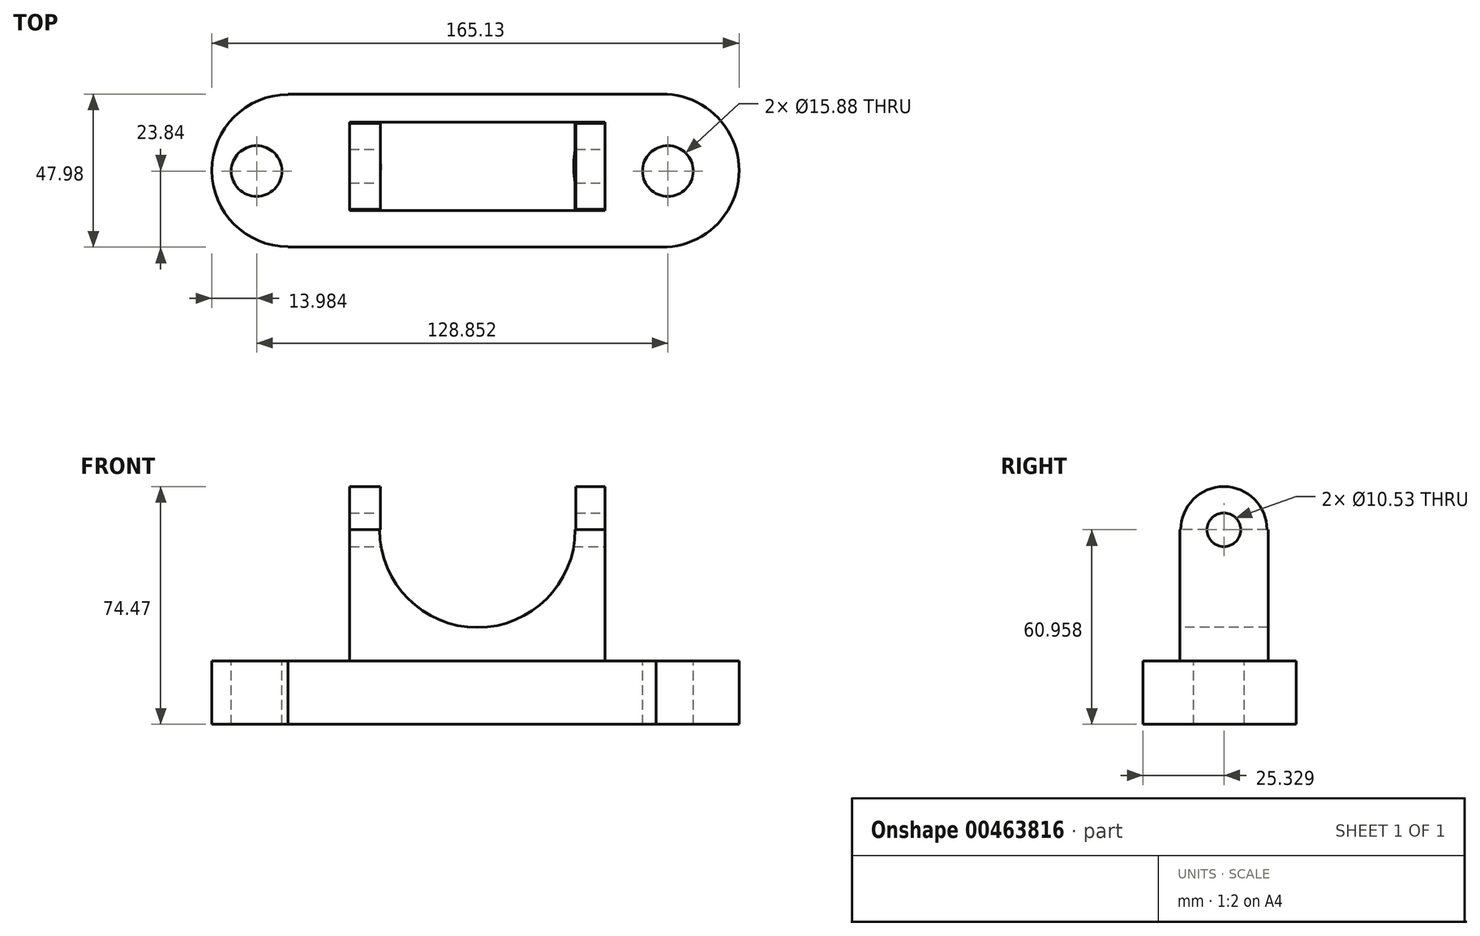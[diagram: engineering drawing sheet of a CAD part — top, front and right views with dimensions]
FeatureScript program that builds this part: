
annotation { "Feature Type Name" : "Feature", "Feature Type Description" : "" }
export const myFeature = defineFeature(function(context is Context, id is Id, definition is map)
    precondition{}
    {
        {
            var Q0;
            Q0=qCreatedBy(makeId("Top.planeOp"),FACE);
            var sketch = newSketch(context, id + "F0", { "sketchPlane" : qUnion([Q0])});
            skLineSegment(sketch, "E0.bottom", {"start": v(-54.58, 24.06) * mm, "end": v(62.72, 24.06) * mm});
            skLineSegment(sketch, "E0.top", {"start": v(-54.58, -23.76) * mm, "end": v(62.72, -23.76) * mm});
            skLineSegment(sketch, "E0.left", {"start": v(-54.58, 24.06) * mm, "end": v(-54.58, -23.76) * mm});
            skLineSegment(sketch, "E0.right", {"start": v(62.72, 24.06) * mm, "end": v(62.72, -23.76) * mm});
            skCircle(sketch, "E1", {"center": v(-54.58, 0.15) * mm, "radius": 23.83 * mm});
            skCircle(sketch, "E2", {"center": v(62.72, 0.15) * mm, "radius": 24 * mm});
            skSolve(sketch);
        }
        {
            var Q0;
            {var subQ0=sQuery(id+"F0.wireOp",EDGE,"E0.right");Q0=makeQuery(id+"F0.imprint","IMPRINT",FACE,{"disambiguationData":[TD([[makeQuery(id+"F0.imprint","IMPRINT",EDGE,{"derivedFrom":subQ0}),-1.0]])]});}
            var Q1;
            {var subQ0=sQuery(id+"F0.wireOp",EDGE,"E0.left");var subQ5=sQuery(id+"F0.wireOp",EDGE,"E0.bottom");var subQ6=makeQuery(id+"F0.imprint","INTERSECT",VERTEX,{"derivedFrom":[subQ5,subQ0]});Q1=makeQuery(id+"F0.imprint","IMPRINT",FACE,{"disambiguationData":[TD([[makeQuery(id+"F0.imprint","IMPRINT",EDGE,{"disambiguationData":[TD([[subQ6,-1.0]])],"derivedFrom":subQ5}),-1.0]])]});}
            var Q2;
            {var subQ0=sQuery(id+"F0.wireOp",EDGE,"E1");var subQ1=sQuery(id+"F0.wireOp",EDGE,"E0.left");var subQ2=makeQuery(id+"F0.imprint","INTERSECT",VERTEX,{"disambiguationData":[OD(0.0)],"derivedFrom":[subQ1,subQ0]});Q2=makeQuery(id+"F0.imprint","IMPRINT",FACE,{"disambiguationData":[TD([[makeQuery(id+"F0.imprint","IMPRINT",EDGE,{"disambiguationData":[TD([[subQ2,-1.0]])],"derivedFrom":subQ1}),-1.0]])]});}
            var Q3;
            {var subQ0=sQuery(id+"F0.wireOp",EDGE,"E0.right");Q3=makeQuery(id+"F0.imprint","IMPRINT",FACE,{"disambiguationData":[TD([[makeQuery(id+"F0.imprint","IMPRINT",EDGE,{"derivedFrom":subQ0}),1.0]])]});}
            var Q4;
            {var subQ0=sQuery(id+"F0.wireOp",EDGE,"E1");var subQ1=sQuery(id+"F0.wireOp",EDGE,"E0.left");var subQ2=makeQuery(id+"F0.imprint","INTERSECT",VERTEX,{"disambiguationData":[OD(0.0)],"derivedFrom":[subQ1,subQ0]});Q4=makeQuery(id+"F0.imprint","IMPRINT",FACE,{"disambiguationData":[TD([[makeQuery(id+"F0.imprint","IMPRINT",EDGE,{"disambiguationData":[TD([[subQ2,-1.0]])],"derivedFrom":subQ1}),1.0]])]});}
            extrude(context, id + "F1", {"entities" : qUnion([Q0, Q1, Q2, Q3, Q4]), "oppositeDirection" : true, "depth" : 19.8 * mm});
        }
        {
            var Q0;
            Q0=makeQuery(id+"F1.opExtrude","CAP_FACE",FACE,{"disambiguationData":[OSD([sQuery(id+"F0.wireOp",EDGE,"E0.bottom"),sQuery(id+"F0.wireOp",EDGE,"E0.top"),sQuery(id+"F0.wireOp",EDGE,"E0.left"),sQuery(id+"F0.wireOp",EDGE,"E1"),sQuery(id+"F0.wireOp",EDGE,"E2")])],"isStart":true});
            var sketch = newSketch(context, id + "F2", { "sketchPlane" : qUnion([Q0])});
            skCircle(sketch, "E3", {"center": v(-64.43, 0) * mm, "radius": 7.94 * mm});
            skCircle(sketch, "E4.MirrorC", {"center": v(64.43, 0) * mm, "radius": 7.94 * mm});
            skSolve(sketch);
        }
        {
            var Q0;
            Q0=makeQuery(id+"F2.imprint","IMPRINT",FACE,{"disambiguationData":[TD([[makeQuery(id+"F2.imprint","IMPRINT",EDGE,{"derivedFrom":sQuery(id+"F2.wireOp",EDGE,"E3")}),1.0]])]});
            extrude(context, id + "F3", {"entities" : qUnion([Q0]), "operationType" : NewBodyOperationType.REMOVE, "oppositeDirection" : true, "depth" : 53.6 * mm});
        }
        {
            var Q0;
            Q0 = qSketchRegion(id + "F2", true);
            extrude(context, id + "F4", {"entities" : qUnion([Q0]), "operationType" : NewBodyOperationType.REMOVE, "oppositeDirection" : true, "depth" : 72.14 * mm});
        }
        {
            var Q0;
            Q0=makeQuery(id+"F1.opExtrude","CAP_FACE",FACE,{"disambiguationData":[OSD([sQuery(id+"F0.wireOp",EDGE,"E0.bottom"),sQuery(id+"F0.wireOp",EDGE,"E0.top"),sQuery(id+"F0.wireOp",EDGE,"E0.left"),sQuery(id+"F0.wireOp",EDGE,"E1"),sQuery(id+"F0.wireOp",EDGE,"E2")])],"isStart":true});
            var sketch = newSketch(context, id + "F5", { "sketchPlane" : qUnion([Q0])});
            skLineSegment(sketch, "E5.bottom", {"start": v(-35.25, 15.31) * mm, "end": v(44.76, 15.31) * mm});
            skLineSegment(sketch, "E5.top", {"start": v(-35.25, -12.34) * mm, "end": v(44.76, -12.34) * mm});
            skLineSegment(sketch, "E5.left", {"start": v(-35.25, 15.31) * mm, "end": v(-35.25, -12.34) * mm});
            skLineSegment(sketch, "E5.right", {"start": v(44.76, 15.31) * mm, "end": v(44.76, -12.34) * mm});
            skSolve(sketch);
        }
        {
            var Q0;
            Q0=makeQuery(id+"F5.imprint","IMPRINT",FACE,{"disambiguationData":[TD([[makeQuery(id+"F5.imprint","IMPRINT",EDGE,{"derivedFrom":sQuery(id+"F5.wireOp",EDGE,"E5.bottom")}),-1.0]])]});
            extrude(context, id + "F6", {"entities" : qUnion([Q0]), "operationType" : NewBodyOperationType.ADD, "depth" : 41.15 * mm});
        }
        {
            var Q0;
            Q0=makeQuery(id+"F6.opExtrude","SWEPT_FACE",FACE,{"disambiguationData":[OSD([sQuery(id+"F5.wireOp",EDGE,"E5.top")])]});
            var sketch = newSketch(context, id + "F7", { "sketchPlane" : qUnion([Q0])});
            skCircle(sketch, "E6", {"center": v(4.76, 41.15) * mm, "radius": 30.63 * mm});
            skSolve(sketch);
        }
        {
            var Q0;
            {var subQ0=sQuery(id+"F7.wireOp",EDGE,"E6");var subQ1=makeQuery(id+"F6.opExtrude","CAP_EDGE",EDGE,{"disambiguationData":[OSD([sQuery(id+"F5.wireOp",EDGE,"E5.top")])],"isStart":false});var subQ2=makeQuery(id+"F7.imprint","INTERSECT",VERTEX,{"disambiguationData":[OD(0.0)],"derivedFrom":[subQ1,subQ0]});Q0=makeQuery(id+"F7.imprint","IMPRINT",FACE,{"disambiguationData":[TD([[makeQuery(id+"F7.imprint","IMPRINT",EDGE,{"disambiguationData":[TD([[subQ2,1.0]])],"derivedFrom":subQ0}),1.0]])]});}
            var Q1;
            {var subQ0=sQuery(id+"F7.wireOp",EDGE,"E6");var subQ1=makeQuery(id+"F6.opExtrude","CAP_EDGE",EDGE,{"disambiguationData":[OSD([sQuery(id+"F5.wireOp",EDGE,"E5.top")])],"isStart":false});var subQ2=makeQuery(id+"F7.imprint","INTERSECT",VERTEX,{"disambiguationData":[OD(0.0)],"derivedFrom":[subQ1,subQ0]});Q1=makeQuery(id+"F7.imprint","IMPRINT",FACE,{"disambiguationData":[TD([[makeQuery(id+"F7.imprint","IMPRINT",EDGE,{"disambiguationData":[TD([[subQ2,-1.0]])],"derivedFrom":subQ0}),1.0]])]});}
            extrude(context, id + "F8", {"entities" : qUnion([Q0, Q1]), "operationType" : NewBodyOperationType.REMOVE, "oppositeDirection" : true, "depth" : 64.52 * mm});
        }
        {
            var Q0;
            Q0=makeQuery(id+"F6.opExtrude","SWEPT_FACE",FACE,{"disambiguationData":[OSD([sQuery(id+"F5.wireOp",EDGE,"E5.left")])]});
            var sketch = newSketch(context, id + "F9", { "sketchPlane" : qUnion([Q0])});
            skCircle(sketch, "E7", {"center": v(-1.49, 41.15) * mm, "radius": 13.46 * mm});
            skSolve(sketch);
        }
        {
            var Q0;
            {var subQ0=sQuery(id+"F9.wireOp",EDGE,"E7");var subQ1=makeQuery(id+"F6.opExtrude","CAP_EDGE",EDGE,{"disambiguationData":[OSD([sQuery(id+"F5.wireOp",EDGE,"E5.left")])],"isStart":false});var subQ2=makeQuery(id+"F9.imprint","INTERSECT",VERTEX,{"disambiguationData":[OD(0.0)],"derivedFrom":[subQ1,subQ0]});Q0=makeQuery(id+"F9.imprint","IMPRINT",FACE,{"disambiguationData":[TD([[makeQuery(id+"F9.imprint","IMPRINT",EDGE,{"disambiguationData":[TD([[subQ2,1.0]])],"derivedFrom":subQ0}),1.0]])]});}
            extrude(context, id + "F10", {"entities" : qUnion([Q0]), "operationType" : NewBodyOperationType.ADD, "oppositeDirection" : true, "depth" : 9.65 * mm});
        }
        {
            var Q0;
            Q0=makeQuery(id+"F6.opExtrude","SWEPT_FACE",FACE,{"disambiguationData":[OSD([sQuery(id+"F5.wireOp",EDGE,"E5.right")])]});
            var sketch = newSketch(context, id + "F11", { "sketchPlane" : qUnion([Q0])});
            skCircle(sketch, "E8", {"center": v(1.49, 41.15) * mm, "radius": 13.5 * mm});
            skSolve(sketch);
        }
        {
            var Q0;
            {var subQ0=sQuery(id+"F11.wireOp",EDGE,"E8");var subQ1=makeQuery(id+"F6.opExtrude","CAP_EDGE",EDGE,{"disambiguationData":[OSD([sQuery(id+"F5.wireOp",EDGE,"E5.right")])],"isStart":false});var subQ2=makeQuery(id+"F11.imprint","INTERSECT",VERTEX,{"disambiguationData":[OD(0.0)],"derivedFrom":[subQ1,subQ0]});Q0=makeQuery(id+"F11.imprint","IMPRINT",FACE,{"disambiguationData":[TD([[makeQuery(id+"F11.imprint","IMPRINT",EDGE,{"disambiguationData":[TD([[subQ2,-1.0]])],"derivedFrom":subQ0}),1.0]])]});}
            extrude(context, id + "F12", {"entities" : qUnion([Q0]), "operationType" : NewBodyOperationType.ADD, "oppositeDirection" : true, "depth" : 9.14 * mm});
        }
        {
            var Q0;
            {var subQ0=sQuery(id+"F5.wireOp",EDGE,"E5.right");Q0=makeQuery(id+"F12.boolean.opBoolean","MERGE",FACE,{"derivedFrom":[makeQuery(id+"F6.opExtrude","SWEPT_FACE",FACE,{"disambiguationData":[OSD([subQ0])]}),makeQuery(id+"F12.opExtrude","CAP_FACE",FACE,{"disambiguationData":[OSD([subQ0,sQuery(id+"F11.wireOp",EDGE,"E8")])],"isStart":true})]});}
            var sketch = newSketch(context, id + "F13", { "sketchPlane" : qUnion([Q0])});
            skCircle(sketch, "E9", {"center": v(1.49, 41.15) * mm, "radius": 5.26 * mm});
            skSolve(sketch);
        }
        {
            var Q0;
            Q0=makeQuery(id+"F13.imprint","IMPRINT",FACE,{"disambiguationData":[TD([[makeQuery(id+"F13.imprint","IMPRINT",EDGE,{"derivedFrom":sQuery(id+"F13.wireOp",EDGE,"E9")}),1.0]])]});
            extrude(context, id + "F14", {"entities" : qUnion([Q0]), "operationType" : NewBodyOperationType.REMOVE, "oppositeDirection" : true, "depth" : 114.05 * mm});
        }
    });
